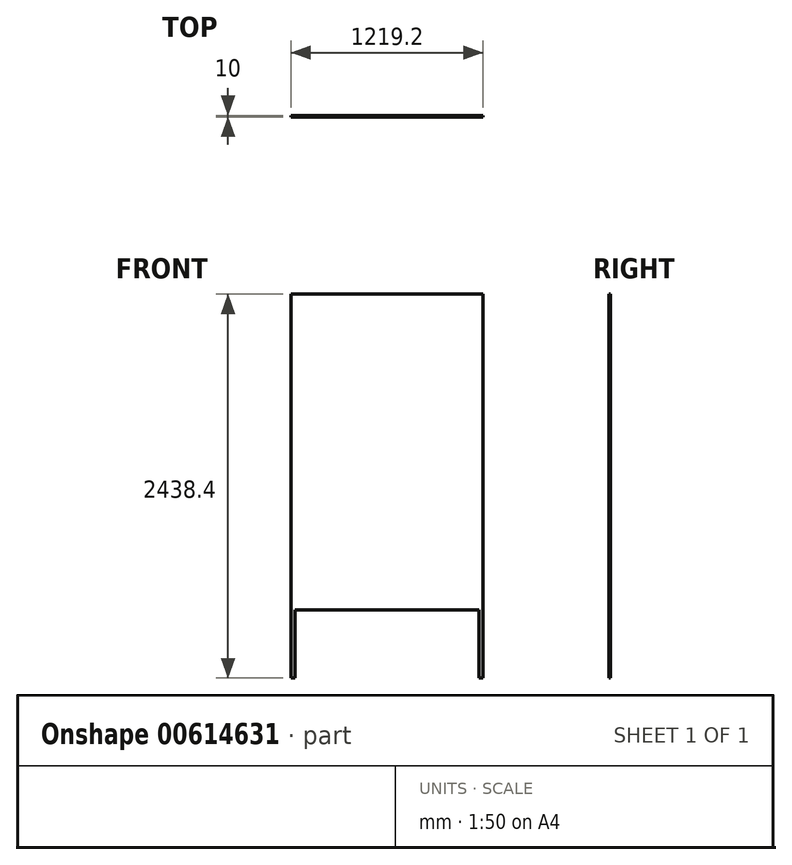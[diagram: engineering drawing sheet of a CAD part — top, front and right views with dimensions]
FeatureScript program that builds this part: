
annotation { "Feature Type Name" : "Feature", "Feature Type Description" : "" }
export const myFeature = defineFeature(function(context is Context, id is Id, definition is map)
    precondition{}
    {
        {
            var Q0;
            Q0=qCreatedBy(makeId("Front.planeOp"),FACE);
            var sketch = newSketch(context, id + "F0", { "sketchPlane" : qUnion([Q0])});
            skLineSegment(sketch, "E0.bottom", {"start": v(609.6, -1219.2) * mm, "end": v(-609.6, -1219.2) * mm});
            skLineSegment(sketch, "E0.top", {"start": v(609.6, 1219.2) * mm, "end": v(-609.6, 1219.2) * mm});
            skLineSegment(sketch, "E0.left", {"start": v(609.6, -1219.2) * mm, "end": v(609.6, 1219.2) * mm});
            skLineSegment(sketch, "E0.right", {"start": v(-609.6, -1219.2) * mm, "end": v(-609.6, 1219.2) * mm});
            skPoint(sketch, "E0.middle", {"position": v(0, 0) * mm});
            skSolve(sketch);
        }
        {
            var Q0;
            Q0=makeQuery(id+"F0.imprint","IMPRINT",FACE,{"disambiguationData":[TD([[makeQuery(id+"F0.imprint","IMPRINT",EDGE,{"derivedFrom":sQuery(id+"F0.wireOp",EDGE,"E0.bottom")}),-1.0]])]});
            extrude(context, id + "F1", {"entities" : qUnion([Q0]), "depth" : 10 * mm});
        }
        {
            var Q0;
            Q0=makeQuery(id+"F1.opExtrude","CAP_FACE",FACE,{"disambiguationData":[OSD([sQuery(id+"F0.wireOp",EDGE,"E0.bottom"),sQuery(id+"F0.wireOp",EDGE,"E0.top"),sQuery(id+"F0.wireOp",EDGE,"E0.left"),sQuery(id+"F0.wireOp",EDGE,"E0.right")])],"isStart":false});
            var sketch = newSketch(context, id + "F2", { "sketchPlane" : qUnion([Q0])});
            skLineSegment(sketch, "E1.bottom", {"start": v(-584.2, -1219.2) * mm, "end": v(584.2, -1219.2) * mm});
            skLineSegment(sketch, "E1.top", {"start": v(-584.2, -787.4) * mm, "end": v(584.2, -787.4) * mm});
            skLineSegment(sketch, "E1.left", {"start": v(-584.2, -1219.2) * mm, "end": v(-584.2, -787.4) * mm});
            skLineSegment(sketch, "E1.right", {"start": v(584.2, -1219.2) * mm, "end": v(584.2, -787.4) * mm});
            skSolve(sketch);
        }
        {
            var Q0;
            Q0=makeQuery(id+"F2.imprint","IMPRINT",FACE,{"disambiguationData":[TD([[makeQuery(id+"F2.imprint","IMPRINT",EDGE,{"derivedFrom":sQuery(id+"F2.wireOp",EDGE,"E1.bottom")}),-1.0]])]});
            extrude(context, id + "F3", {"entities" : qUnion([Q0]), "operationType" : NewBodyOperationType.REMOVE, "endBound" : BoundingType.THROUGH_ALL, "oppositeDirection" : true, "depth" : 25.4 * mm, "offsetDistance" : 25.4 * mm});
        }
    });
